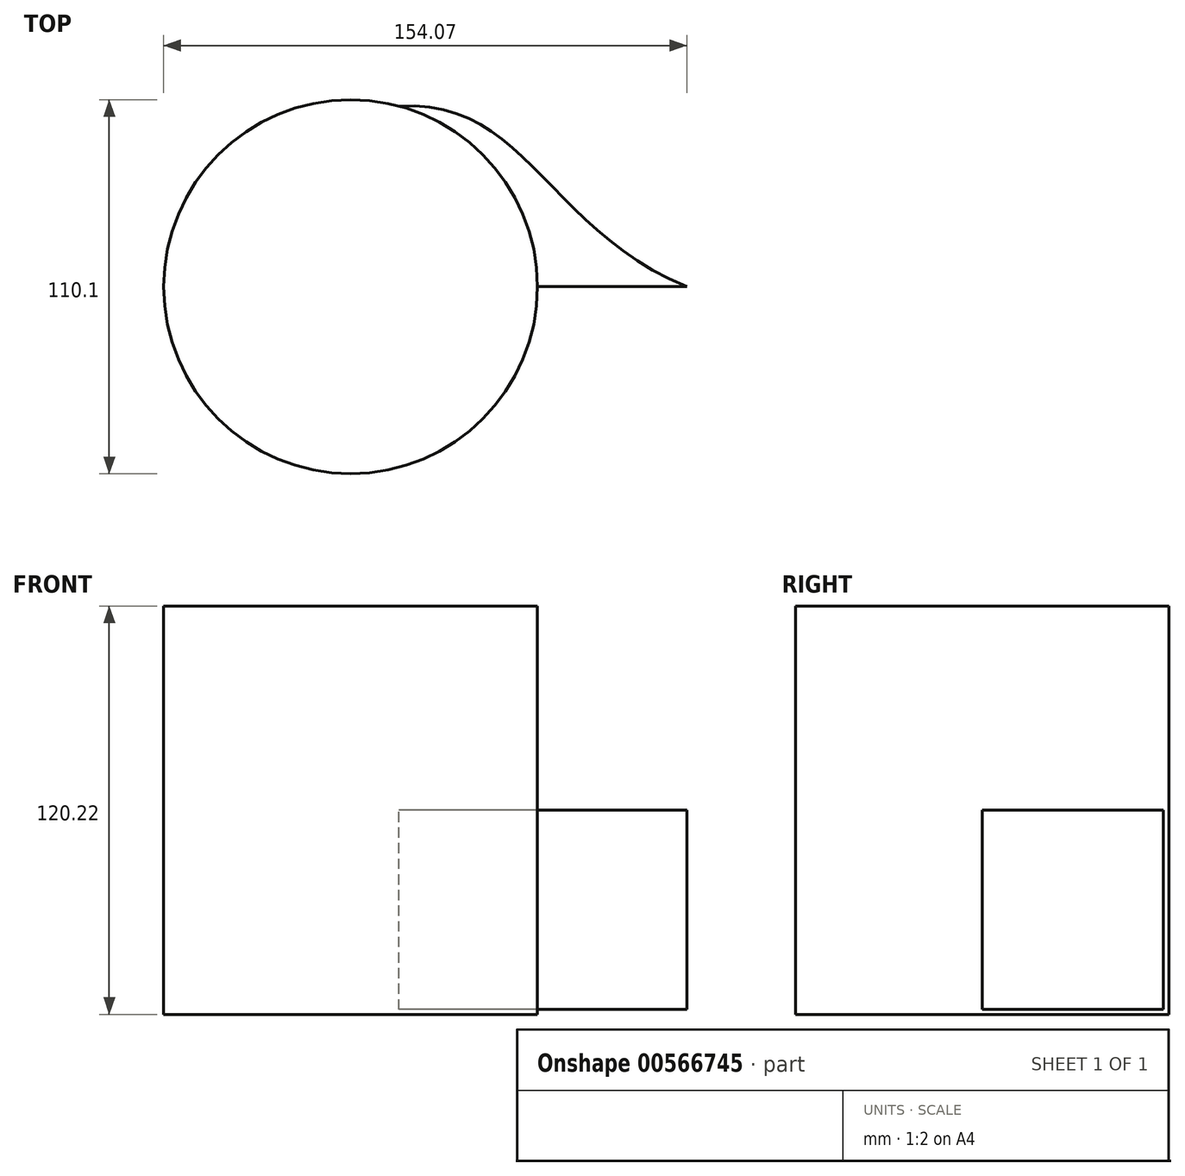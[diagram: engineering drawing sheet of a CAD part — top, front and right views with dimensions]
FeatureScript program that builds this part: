
annotation { "Feature Type Name" : "Feature", "Feature Type Description" : "" }
export const myFeature = defineFeature(function(context is Context, id is Id, definition is map)
    precondition{}
    {
        {
            var Q0;
            Q0=qCreatedBy(makeId("Front.planeOp"),FACE);
            var sketch = newSketch(context, id + "F0", { "sketchPlane" : qUnion([Q0])});
            skLineSegment(sketch, "E0.bottom", {"start": v(27.52, 60.1) * mm, "end": v(-27.52, 60.1) * mm});
            skLineSegment(sketch, "E0.top", {"start": v(27.52, -60.1) * mm, "end": v(-27.52, -60.1) * mm});
            skLineSegment(sketch, "E0.left", {"start": v(27.52, 60.1) * mm, "end": v(27.52, -60.1) * mm});
            skLineSegment(sketch, "E0.right", {"start": v(-27.52, 60.1) * mm, "end": v(-27.52, -60.1) * mm});
            skPoint(sketch, "E0.middle", {"position": v(0, 0) * mm});
            skLineSegment(sketch, "E1", {"start": v(27.52, 37.01) * mm, "end": v(71.5, 0) * mm});
            skLineSegment(sketch, "E2", {"start": v(71.5, 0) * mm, "end": v(71.5, -54.73) * mm});
            skLineSegment(sketch, "E3", {"start": v(71.5, -54.73) * mm, "end": v(27.52, -54.73) * mm});
            skLineSegment(sketch, "E4", {"start": v(27.52, -54.73) * mm, "end": v(27.52, 37.01) * mm});
            skSolve(sketch);
        }
        {
            var Q0;
            {var subQ3=sQuery(id+"F0.wireOp",EDGE,"E0.bottom");Q0=makeQuery(id+"F0.imprint","IMPRINT",FACE,{"disambiguationData":[TD([[makeQuery(id+"F0.imprint","IMPRINT",EDGE,{"derivedFrom":subQ3}),1.0]])]});}
            var Q1;
            Q1=sQuery(id+"F0.wireOp",EDGE,"E0.right");
            revolve(context, id + "F1", {"entities" : qUnion([Q0]), "axis" : qUnion([Q1]), "revolveType" : RevolveType.FULL});
        }
        {
            var Q0;
            Q0=qCreatedBy(makeId("Top.planeOp"),FACE);
            var sketch = newSketch(context, id + "F2", { "sketchPlane" : qUnion([Q0])});
            skFitSpline(sketch, "E5", {"points": [v(71.5, 0) * mm, v(-13.31, 53.2) * mm], "startDerivative": vector(-124.34, 51.88) * mm, "endDerivative": vector(-111.73, -6.78) * mm});
            skLineSegment(sketch, "E6", {"start": v(71.5, 0) * mm, "end": v(0, 0) * mm});
            skLineSegment(sketch, "E7", {"start": v(0, 0) * mm, "end": v(-13.31, 53.2) * mm});
            skSolve(sketch);
        }
        {
            var Q0;
            Q0=makeQuery(id+"F2.imprint","IMPRINT",FACE,{"disambiguationData":[TD([[makeQuery(id+"F2.imprint","IMPRINT",EDGE,{"derivedFrom":sQuery(id+"F2.wireOp",EDGE,"E5")}),1.0]])]});
            extrude(context, id + "F3", {"entities" : qUnion([Q0]), "operationType" : NewBodyOperationType.ADD, "oppositeDirection" : true, "depth" : 58.67 * mm, "offsetDistance" : 25.4 * mm});
        }
    });
